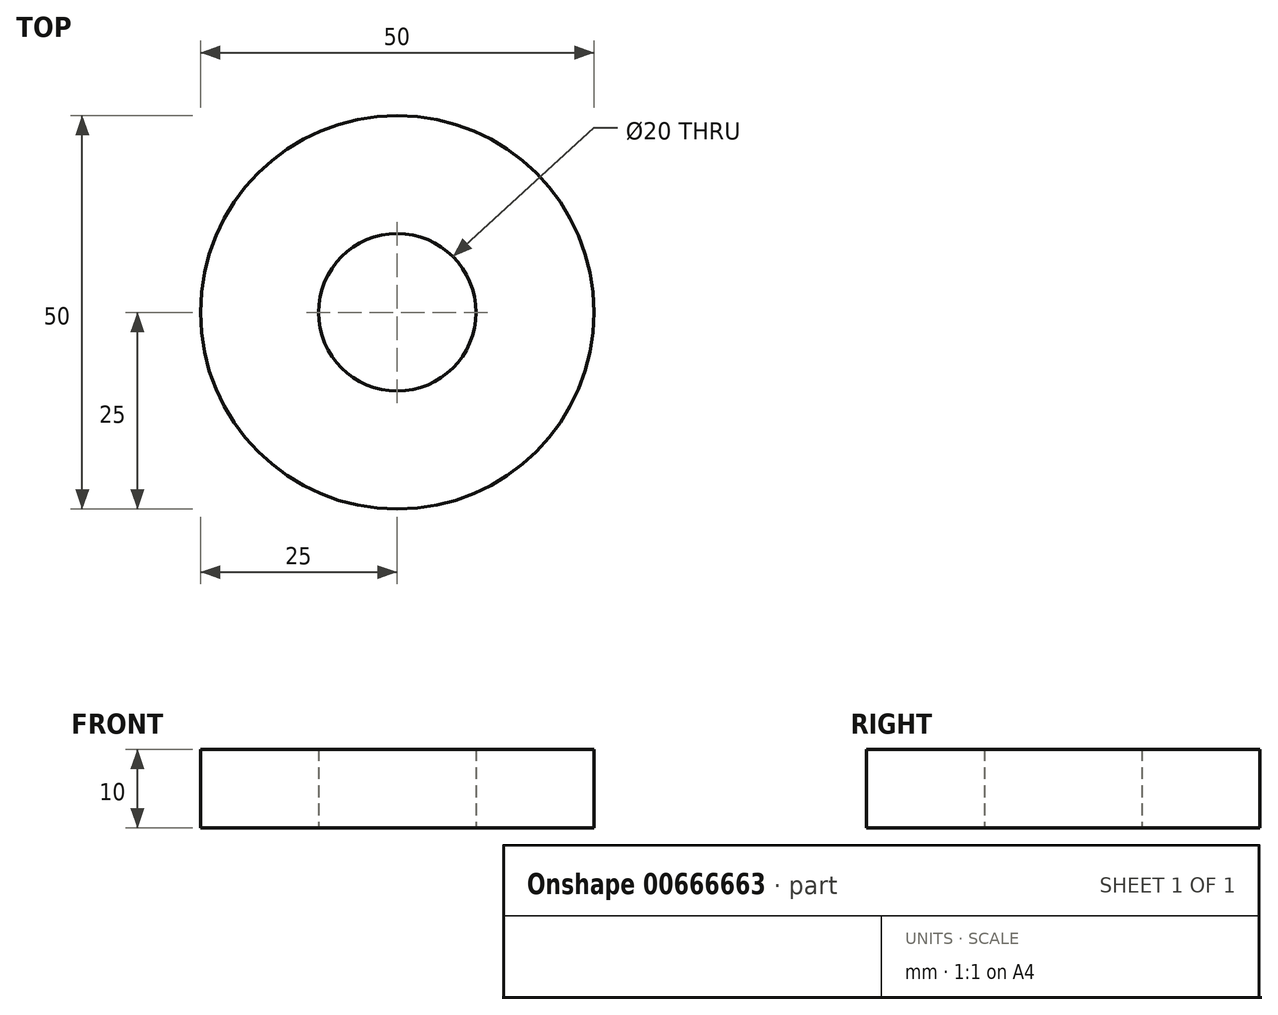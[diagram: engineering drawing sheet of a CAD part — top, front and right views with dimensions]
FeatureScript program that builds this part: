
annotation { "Feature Type Name" : "Feature", "Feature Type Description" : "" }
export const myFeature = defineFeature(function(context is Context, id is Id, definition is map)
    precondition{}
    {
        {
            var Q0;
            Q0=qCreatedBy(makeId("Top.planeOp"),FACE);
            var sketch = newSketch(context, id + "F0", { "sketchPlane" : qUnion([Q0])});
            skCircle(sketch, "E0", {"center": v(0, 0) * mm, "radius": 25 * mm});
            skCircle(sketch, "E1", {"center": v(0, 0) * mm, "radius": 10 * mm});
            skSolve(sketch);
        }
        {
            var Q0;
            Q0 = qSketchRegion(id + "F0", true);
            extrude(context, id + "F1", {"entities" : qUnion([Q0]), "depth" : 10 * mm, "offsetDistance" : 25 * mm});
        }
    });
